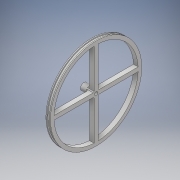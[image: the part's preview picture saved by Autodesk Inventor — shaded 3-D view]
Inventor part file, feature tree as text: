
AUTODESK INVENTOR PART (.ipt)
format: ipt  version: 2018 (Build 220112000, 112)  size: 202,752 bytes
history: native  units: mm
features: extrude x12, sketch x12, pattern_circular x1, fillet x1
ambient origin geometry x8: Origin, YZ Plane, XZ Plane, XY Plane, X Axis, Y Axis, Z Axis, Center Point
bodies: Solid1 (feature_tree)
feature tree (26):
  extrude  "Extrusion1"  Depth=3.5mm TaperAngle=0.0deg
  extrude  "Extrusion2"  Depth=1.0mm TaperAngle=0.0deg
  extrude  "Extrusion3"  Depth=1.0mm TaperAngle=0.0deg
  extrude  "Extrusion4"  Depth=6.0mm TaperAngle=0.0deg
  extrude  "Extrusion5"  Depth=10.0mm TaperAngle=0.0deg
  extrude  "Extrusion6"  Depth=1.0mm TaperAngle=0.0deg
  extrude  "Extrusion7"  Depth=1.0mm
  extrude  "Extrusion8"  Depth=4.0mm
  extrude  "Extrusion9"  Depth=40.0mm TaperAngle=360.0deg
  extrude  "Extrusion10"  Depth=2.0mm TaperAngle=0.0deg
  pattern_circular  "Circular Pattern1"  [2 undecoded]
  fillet  "Fillet1"  [1 undecoded]
  extrude  "Extrusion11"  [1 undecoded]
  extrude  "Extrusion12"  [1 undecoded]
  sketch  "Sketch1"  dims[d0=88.0mm d1=3.5mm d2=0.0mm]
  sketch  "Sketch2"  dims[d3=90.0mm d4=1.0mm d5=0.0mm]
  sketch  "Sketch3"  dims[d6=90.0mm d7=1.0mm d8=0.0mm]
  sketch  "Sketch4"  dims[d9=83.0mm d10=6.0mm d11=0.0mm]
  sketch  "Sketch5"  dims[d12=7.0mm d13=10.0mm d14=0.0mm]
  sketch  "Sketch6"  dims[d15=2.0mm d16=0.0mm d17=1.0mm d18=0.0mm]
  sketch  "Sketch7"  dims[d19=1.0mm d20=0.0mm d21=3.25mm]
  sketch  "Sketch8"  dims[d22=10.0mm d23=0.0mm d24=4.0mm]
  sketch  "Sketch9"  dims[d25=4.5mm d26=0.0mm d27=40.0mm d28=360.0deg]
  sketch  "Sketch10"  dims[d30=2.0mm d31=2.0mm d32=0.0mm]
  sketch  "Sketch11"  dims[d33=1.0mm d34=0.0mm]
  sketch  "Sketch12"
note: 5 required parameter values undecoded (feature->parameter linkage not recoverable at this tier; creation-order binding heuristic only, values carry confidence <= 0.55)
